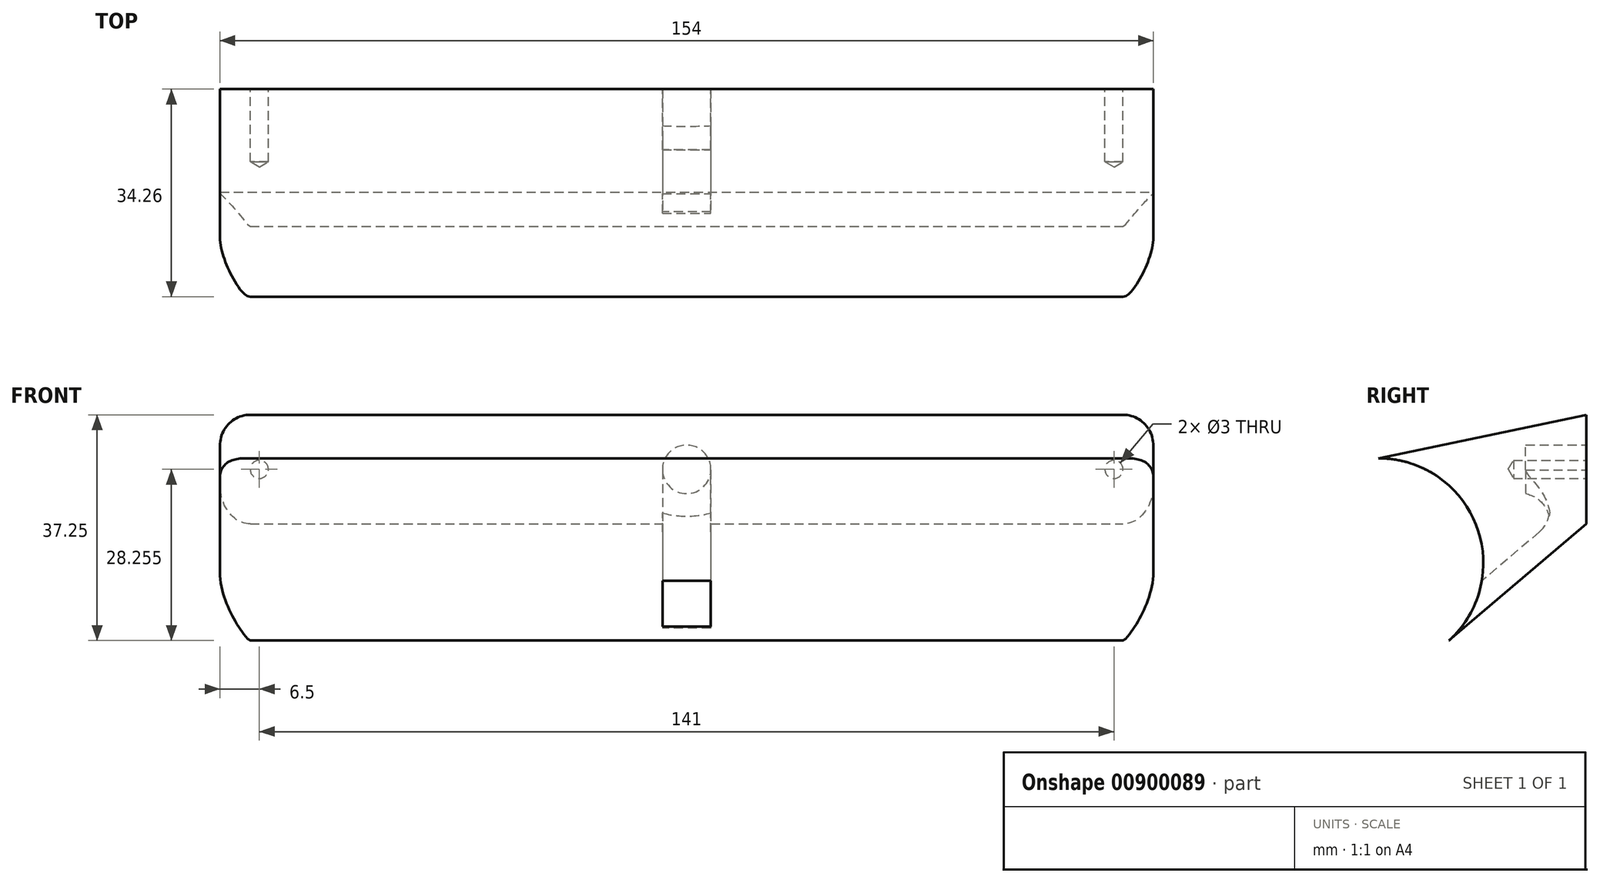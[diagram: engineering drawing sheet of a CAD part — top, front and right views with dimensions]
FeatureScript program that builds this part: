
annotation { "Feature Type Name" : "Feature", "Feature Type Description" : "" }
export const myFeature = defineFeature(function(context is Context, id is Id, definition is map)
    precondition{}
    {
        {
            var Q0;
            Q0=qCreatedBy(makeId("Right.planeOp"),FACE);
            var sketch = newSketch(context, id + "F0", { "sketchPlane" : qUnion([Q0])});
            skArc(sketch, "E0", {"start": v(11.6, -12.8) * mm, "mid": v(16.12, 6.22) * mm, "end": v(0, 17.28) * mm});
            skLineSegment(sketch, "E1", {"start": v(0, 0) * mm, "end": v(0, 17.28) * mm, "construction": true});
            skLineSegment(sketch, "E2", {"start": v(0, 17.28) * mm, "end": v(0, -17.28) * mm, "construction": true});
            skLineSegment(sketch, "E3", {"start": v(0, 17.28) * mm, "end": v(34.26, 24.45) * mm});
            skLineSegment(sketch, "E4", {"start": v(11.6, -12.8) * mm, "end": v(34.26, 6.45) * mm});
            skLineSegment(sketch, "E5", {"start": v(34.26, 6.45) * mm, "end": v(34.26, 24.45) * mm});
            skLineSegment(sketch, "E6", {"start": v(0, 0) * mm, "end": v(0, 54.11) * mm, "construction": true});
            skSolve(sketch);
        }
        {
            var Q0;
            Q0=makeQuery(id+"F0.imprint","IMPRINT",FACE,{"disambiguationData":[TD([[makeQuery(id+"F0.imprint","IMPRINT",EDGE,{"derivedFrom":sQuery(id+"F0.wireOp",EDGE,"E0")}),-1.0]])]});
            extrude(context, id + "F1", {"entities" : qUnion([Q0]), "endBound" : BoundingType.SYMMETRIC, "oppositeDirection" : true, "depth" : 154 * mm, "offsetDistance" : 25 * mm});
        }
        {
            var Q0;
            Q0=makeQuery(id+"F1.opExtrude","SWEPT_FACE",FACE,{"disambiguationData":[OSD([sQuery(id+"F0.wireOp",EDGE,"E5")])]});
            var sketch = newSketch(context, id + "F2", { "sketchPlane" : qUnion([Q0])});
            skLineSegment(sketch, "E7", {"start": v(0, 24.45) * mm, "end": v(0, 6.45) * mm, "construction": true});
            skLineSegment(sketch, "E8", {"start": v(0, 15.45) * mm, "end": v(70.5, 15.45) * mm, "construction": true});
            skLineSegment(sketch, "E9", {"start": v(0, 15.45) * mm, "end": v(-70.5, 15.45) * mm, "construction": true});
            skCircle(sketch, "E10", {"center": v(0, 15.45) * mm, "radius": 4 * mm});
            skSolve(sketch);
        }
        {
            var Q0;
            Q0=sQuery(id+"F2.wireOp",VERTEX,"E9.end");
            var Q1;
            Q1=sQuery(id+"F2.wireOp",VERTEX,"E8.end");
            var Q2;
            Q2=makeQuery(id+"F1.opExtrude","SWEPT_BODY",BODY,{"disambiguationData":[OSD([sQuery(id+"F0.wireOp",EDGE,"E0"),sQuery(id+"F0.wireOp",EDGE,"E3"),sQuery(id+"F0.wireOp",EDGE,"E4"),sQuery(id+"F0.wireOp",EDGE,"E5")])]});
            hole(context, id + "F3", {"style" : HoleStyle.SIMPLE, "endStyle" : HoleEndStyle.BLIND, "holeDiameter" : 3 * mm, "majorDiameter" : 5 * mm, "holeDepth" : 12 * mm, "isTappedThrough" : true, "tappedDepth" : 12 * mm, "tapClearance" : 3, "locations" : qUnion([Q0, Q1]), "scope" : qUnion([Q2])});
        }
        {
            var Q0;
            Q0=makeQuery(id+"F1.opExtrude","CAP_EDGE",EDGE,{"disambiguationData":[OSD([sQuery(id+"F0.wireOp",EDGE,"E3")])],"isStart":true});
            var Q1;
            Q1=makeQuery(id+"F1.opExtrude","CAP_EDGE",EDGE,{"disambiguationData":[OSD([sQuery(id+"F0.wireOp",EDGE,"E4")])],"isStart":true});
            var Q2;
            Q2=makeQuery(id+"F1.opExtrude","CAP_EDGE",EDGE,{"disambiguationData":[OSD([sQuery(id+"F0.wireOp",EDGE,"E3")])],"isStart":false});
            var Q3;
            Q3=makeQuery(id+"F1.opExtrude","CAP_EDGE",EDGE,{"disambiguationData":[OSD([sQuery(id+"F0.wireOp",EDGE,"E4")])],"isStart":false});
            fillet(context, id + "F4", {"entities" : qUnion([Q0, Q1, Q2, Q3]), "radius" : 5 * mm, "tangentPropagation" : true, "allowEdgeOverflow" : false});
        }
        {
            var Q0;
            Q0=makeQuery(id+"F2.imprint","IMPRINT",FACE,{"disambiguationData":[TD([[makeQuery(id+"F2.imprint","IMPRINT",EDGE,{"derivedFrom":sQuery(id+"F2.wireOp",EDGE,"E10")}),1.0]])]});
            extrude(context, id + "F5", {"entities" : qUnion([Q0]), "operationType" : NewBodyOperationType.REMOVE, "oppositeDirection" : true, "depth" : 10 * mm, "offsetDistance" : 25 * mm});
        }
        {
            var Q0;
            Q0=makeQuery(id+"F2.imprint","IMPRINT",FACE,{"disambiguationData":[TD([[makeQuery(id+"F2.imprint","IMPRINT",EDGE,{"derivedFrom":sQuery(id+"F2.wireOp",EDGE,"E10")}),-1.0]])]});
            var sketch = newSketch(context, id + "F6", { "sketchPlane" : qUnion([Q0])});
            skCircle(sketch, "E11.0", {"center": v(0, 15.45) * mm, "radius": 4 * mm});
            skLineSegment(sketch, "E12", {"start": v(-4, 15.33) * mm, "end": v(-4, 6.45) * mm});
            skLineSegment(sketch, "E13.MirrorCS", {"start": v(4, 15.33) * mm, "end": v(4, 6.45) * mm});
            skLineSegment(sketch, "E14", {"start": v(-4, 6.45) * mm, "end": v(4, 6.45) * mm});
            skLineSegment(sketch, "E15", {"start": v(-4, 15.33) * mm, "end": v(4, 15.33) * mm});
            skSolve(sketch);
        }
        {
            var Q0;
            Q0 = qSketchRegion(id + "F6", true);
            extrude(context, id + "F7", {"entities" : qUnion([Q0]), "operationType" : NewBodyOperationType.REMOVE, "oppositeDirection" : true, "depth" : 6 * mm, "offsetDistance" : 25 * mm});
        }
        {
            var Q0;
            Q0=makeQuery(id+"F1.opExtrude","SWEPT_FACE",FACE,{"disambiguationData":[OSD([sQuery(id+"F0.wireOp",EDGE,"E4")])]});
            var sketch = newSketch(context, id + "F8", { "sketchPlane" : qUnion([Q0])});
            skLineSegment(sketch, "E16", {"start": v(4, -30.28) * mm, "end": v(4, -3.7) * mm});
            skLineSegment(sketch, "E17", {"start": v(4, -3.7) * mm, "end": v(-4, -3.7) * mm});
            skLineSegment(sketch, "E18", {"start": v(-4, -30.28) * mm, "end": v(-4, -3.7) * mm});
            skPoint(sketch, "E19.0.start.orphan", {"position": v(-4, -36.03) * mm});
            skPoint(sketch, "E20.0.start.orphan", {"position": v(4, -36.03) * mm});
            skLineSegment(sketch, "E21", {"start": v(4, -30.28) * mm, "end": v(-4, -30.28) * mm});
            skSolve(sketch);
        }
        {
            var Q0;
            {var subQ0=sQuery(id+"F8.wireOp",EDGE,"E17");Q0=makeQuery(id+"F8.imprint","IMPRINT",FACE,{"disambiguationData":[TD([[makeQuery(id+"F8.imprint","IMPRINT",EDGE,{"derivedFrom":subQ0}),1.0]])]});}
            extrude(context, id + "F9", {"entities" : qUnion([Q0]), "operationType" : NewBodyOperationType.REMOVE, "oppositeDirection" : true, "depth" : 4 * mm, "offsetDistance" : 25 * mm});
        }
        {
            var Q0;
            Q0=makeQuery(id+"F7.boolean.opBoolean","INTERSECT",EDGE,{"derivedFrom":[makeQuery(id+"F5.boolean.opBoolean","COPY",FACE,{"derivedFrom":makeQuery(id+"F5.opExtrude","SWEPT_FACE",FACE,{"disambiguationData":[OSD([sQuery(id+"F2.wireOp",EDGE,"E10")])]})}),makeQuery(id+"F7.opExtrude","CAP_FACE",FACE,{"disambiguationData":[OSD([sQuery(id+"F6.wireOp",EDGE,"E11.0"),sQuery(id+"F6.wireOp",EDGE,"E12"),sQuery(id+"F6.wireOp",EDGE,"E13.MirrorCS"),sQuery(id+"F6.wireOp",EDGE,"E14")])],"isStart":false})]});
            var Q1;
            Q1=makeQuery(id+"F9.boolean.opBoolean","INTERSECT",EDGE,{"derivedFrom":[makeQuery(id+"F7.boolean.opBoolean","COPY",FACE,{"derivedFrom":makeQuery(id+"F7.opExtrude","CAP_FACE",FACE,{"disambiguationData":[OSD([sQuery(id+"F6.wireOp",EDGE,"E11.0"),sQuery(id+"F6.wireOp",EDGE,"E12"),sQuery(id+"F6.wireOp",EDGE,"E13.MirrorCS"),sQuery(id+"F6.wireOp",EDGE,"E14")])],"isStart":false})}),makeQuery(id+"F9.opExtrude","CAP_FACE",FACE,{"disambiguationData":[OSD([sQuery(id+"F8.wireOp",EDGE,"E16"),sQuery(id+"F8.wireOp",EDGE,"E17"),sQuery(id+"F8.wireOp",EDGE,"E18"),sQuery(id+"F8.wireOp",EDGE,"E21")])],"isStart":false})]});
            fillet(context, id + "F10", {"entities" : qUnion([Q0, Q1]), "radius" : 5 * mm, "tangentPropagation" : true, "allowEdgeOverflow" : false});
        }
    });
